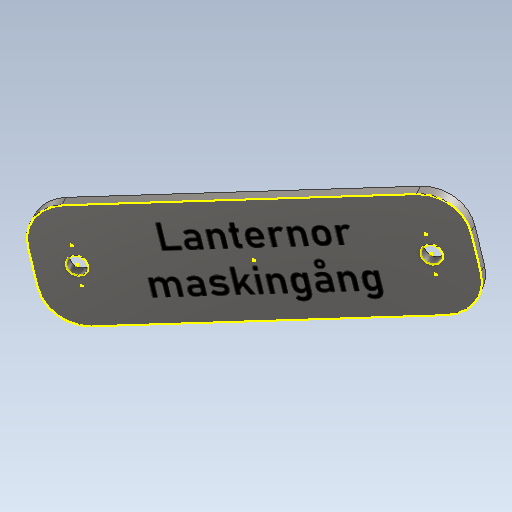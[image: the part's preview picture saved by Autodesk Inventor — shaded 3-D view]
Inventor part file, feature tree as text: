
AUTODESK INVENTOR PART (.ipt)
format: ipt  version: 2021 (Build 250183000, 183)  size: 135,680 bytes
history: native  units: mm
features: sketch x5, extrude x2, fillet x1, projected_geometry x1
ambient origin geometry x8: Origin, YZ Plane, XZ Plane, XY Plane, X Axis, Y Axis, Z Axis, Center Point
bodies: Solid1 (feature_tree)
feature tree (9):
  extrude  "Extrusion1"  Depth=15.0mm
  extrude  "Extrusion2"  Depth=5.0mm
  fillet  "Fillet1"  Radius=5.0mm
  sketch  "Sketch3"  dims[d6=1.5mm d7=0.0mm]
  sketch  "Sketch4"  dims[d8=5.0mm]
  sketch  "Sketch5"
  sketch  "Sketch1"  dims[d0=50.0mm d1=15.0mm]
  sketch  "Sketch2"  dims[d2=1.5mm d3=0.0mm d4=2.5mm d5=5.0mm]
  projected_geometry  "Projected Loop1"
